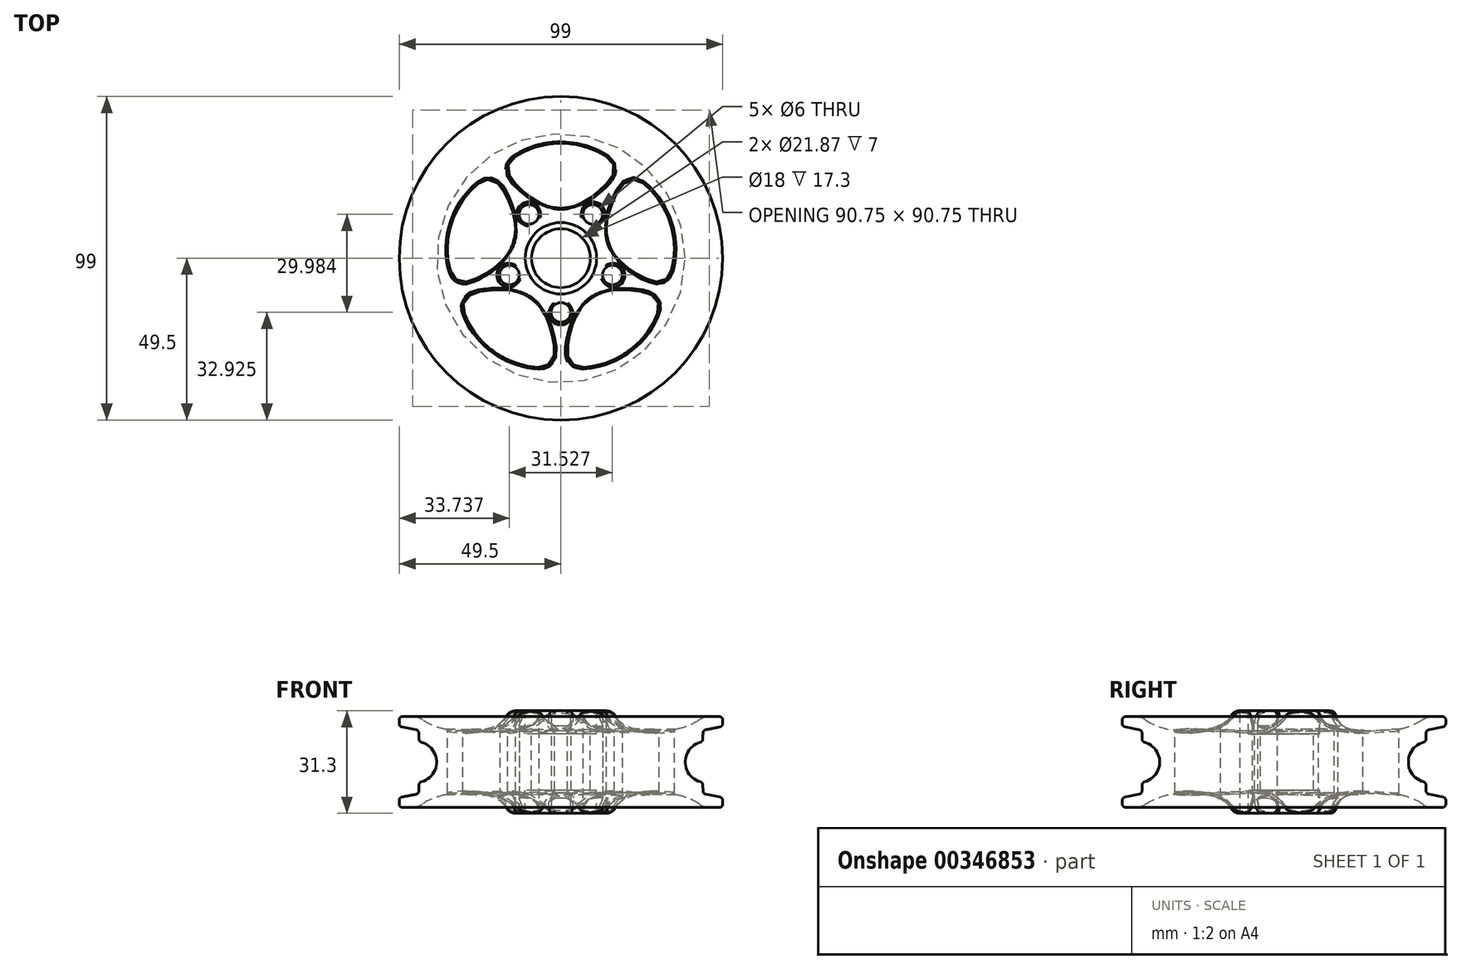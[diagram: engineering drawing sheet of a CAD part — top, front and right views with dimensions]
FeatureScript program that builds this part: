
annotation { "Feature Type Name" : "Feature", "Feature Type Description" : "" }
export const myFeature = defineFeature(function(context is Context, id is Id, definition is map)
    precondition{}
    {
        {
            var Q0;
            Q0=qCreatedBy(makeId("Front.planeOp"),FACE);
            var sketch = newSketch(context, id + "F0", { "sketchPlane" : qUnion([Q0])});
            skLineSegment(sketch, "E0", {"start": v(-10.94, 0) * mm, "end": v(-10.94, 7) * mm});
            skLineSegment(sketch, "E1", {"start": v(-10.94, 24.3) * mm, "end": v(-10.94, 31.3) * mm});
            skLineSegment(sketch, "E2", {"start": v(-10.94, 7) * mm, "end": v(-9, 7) * mm});
            skLineSegment(sketch, "E3", {"start": v(-9, 7) * mm, "end": v(-9, 24.3) * mm});
            skLineSegment(sketch, "E4", {"start": v(-9, 24.3) * mm, "end": v(-10.94, 24.3) * mm});
            skLineSegment(sketch, "E5", {"start": v(-10.94, 31.3) * mm, "end": v(-15.94, 31.3) * mm});
            skLineSegment(sketch, "E6", {"start": v(-10.94, 0) * mm, "end": v(-15.94, 0) * mm});
            skLineSegment(sketch, "E7", {"start": v(-55.59, 1.75) * mm, "end": v(-51.93, 1.75) * mm, "construction": true});
            skLineSegment(sketch, "E8", {"start": v(-9, 15.65) * mm, "end": v(-60.78, 15.65) * mm, "construction": true});
            skLineSegment(sketch, "E9", {"start": v(-55.59, 29.55) * mm, "end": v(-37.99, 29.55) * mm, "construction": true});
            skLineSegment(sketch, "E10", {"start": v(-49.5, 1.75) * mm, "end": v(-43.5, 1.75) * mm});
            skLineSegment(sketch, "E11", {"start": v(-49.5, 1.75) * mm, "end": v(-49.5, 4.75) * mm});
            skLineSegment(sketch, "E12", {"start": v(-49.5, 4.75) * mm, "end": v(-43.5, 5.95) * mm});
            skLineSegment(sketch, "E13", {"start": v(-43.5, 5.95) * mm, "end": v(-43.4, 9.45) * mm});
            skLineSegment(sketch, "E14.MirrorCS", {"start": v(-9, -12.15) * mm, "end": v(-60.78, -12.15) * mm, "construction": true});
            skLineSegment(sketch, "E15.MirrorCS", {"start": v(-43.5, 25.35) * mm, "end": v(-43.4, 21.85) * mm});
            skLineSegment(sketch, "E16.MirrorCS", {"start": v(-49.5, 26.55) * mm, "end": v(-43.5, 25.35) * mm});
            skLineSegment(sketch, "E17.MirrorCS", {"start": v(-49.5, 29.55) * mm, "end": v(-49.5, 26.55) * mm});
            skLineSegment(sketch, "E18.MirrorCS", {"start": v(-49.5, 29.55) * mm, "end": v(-43.5, 29.55) * mm});
            skLineSegment(sketch, "E19", {"start": v(-38.05, 37.76) * mm, "end": v(-38.05, -5.34) * mm, "construction": true});
            skFitSpline(sketch, "E20", {"points": [v(-15.94, 0) * mm, v(-19.3, 4.16) * mm, v(-30.57, 6.15) * mm, v(-38.05, 4.9) * mm, v(-43.5, 1.75) * mm], "startDerivative": vector(-4.85, 18.9) * mm, "endDerivative": vector(-18.06, -19.28) * mm});
            skFitSpline(sketch, "E21.MirrorCS", {"points": [v(-15.94, 31.3) * mm, v(-19.3, 27.14) * mm, v(-30.57, 25.15) * mm, v(-38.05, 26.4) * mm, v(-43.5, 29.55) * mm], "startDerivative": vector(-4.85, -18.9) * mm, "endDerivative": vector(-18.06, 19.28) * mm});
            skArc(sketch, "E22", {"start": v(-43.4, 9.45) * mm, "mid": v(-38.04, 15.65) * mm, "end": v(-43.4, 21.85) * mm});
            skLineSegment(sketch, "E23", {"start": v(0, 53.2) * mm, "end": v(0, -22.44) * mm, "construction": true});
            skSolve(sketch);
        }
        {
            var Q0;
            Q0 = qSketchRegion(id + "F0", true);
            var Q1;
            Q1=makeQuery(id+"F0.imprint","IMPRINT",FACE,{"disambiguationData":[TD([[makeQuery(id+"F0.imprint","IMPRINT",EDGE,{"derivedFrom":sQuery(id+"F0.wireOp",EDGE,"E0")}),1.0]])]});
            var Q2;
            Q2=sQuery(id+"F0.wireOp",EDGE,"E23");
            revolve(context, id + "F1", {"entities" : qUnion([Q0, Q1]), "axis" : qUnion([Q2]), "revolveType" : RevolveType.FULL});
        }
        {
            var Q0;
            Q0=qCreatedBy(makeId("Top.planeOp"),FACE);
            var sketch = newSketch(context, id + "F2", { "sketchPlane" : qUnion([Q0])});
            skPoint(sketch, "E24.center", {"position": v(0, -0.06) * mm});
            skLineSegment(sketch, "E25", {"start": v(0, 56.77) * mm, "end": v(0, 52.22) * mm, "construction": true});
            skFitSpline(sketch, "E26", {"points": [v(5.43, 34.62) * mm, v(-5.43, 34.62) * mm, v(-13.13, 31.63) * mm, v(-15.9, 29.08) * mm, v(-16.02, 25.78) * mm, v(-11.93, 20.8) * mm, v(-5.51, 16.45) * mm, v(0, 15.38) * mm, v(5.51, 16.45) * mm, v(11.93, 20.8) * mm, v(16.02, 25.78) * mm, v(15.9, 29.08) * mm, v(13.13, 31.63) * mm, v(5.43, 34.62) * mm]});
            skFitSpline(sketch, "E27", {"points": [v(34.6, 5.53) * mm, v(31.25, 15.86) * mm, v(26.02, 22.26) * mm, v(22.74, 24.12) * mm, v(19.57, 23.2) * mm, v(16.1, 17.78) * mm, v(13.94, 10.32) * mm, v(14.63, 4.75) * mm, v(17.34, -0.16) * mm, v(23.47, -4.92) * mm, v(29.47, -7.27) * mm, v(32.57, -6.14) * mm, v(34.14, -2.71) * mm, v(34.6, 5.53) * mm]});
            skFitSpline(sketch, "E28", {"points": [v(15.96, -31.2) * mm, v(24.74, -24.82) * mm, v(29.21, -17.87) * mm, v(29.96, -14.18) * mm, v(28.12, -11.44) * mm, v(21.88, -9.82) * mm, v(14.13, -10.07) * mm, v(9.04, -12.44) * mm, v(5.2, -16.55) * mm, v(2.57, -23.85) * mm, v(2.2, -30.28) * mm, v(4.22, -32.88) * mm, v(7.97, -33.3) * mm, v(15.96, -31.2) * mm]});
            skFitSpline(sketch, "E29", {"points": [v(-31.25, 15.86) * mm, v(-34.6, 5.53) * mm, v(-34.14, -2.71) * mm, v(-32.57, -6.14) * mm, v(-29.47, -7.27) * mm, v(-23.47, -4.92) * mm, v(-17.34, -0.16) * mm, v(-14.63, 4.75) * mm, v(-13.94, 10.32) * mm, v(-16.1, 17.78) * mm, v(-19.57, 23.2) * mm, v(-22.74, 24.12) * mm, v(-26.02, 22.26) * mm, v(-31.25, 15.86) * mm]});
            skFitSpline(sketch, "E30", {"points": [v(-24.74, -24.82) * mm, v(-15.96, -31.2) * mm, v(-7.97, -33.3) * mm, v(-4.22, -32.88) * mm, v(-2.2, -30.28) * mm, v(-2.57, -23.85) * mm, v(-5.2, -16.55) * mm, v(-9.04, -12.44) * mm, v(-14.13, -10.07) * mm, v(-21.88, -9.82) * mm, v(-28.12, -11.44) * mm, v(-29.96, -14.18) * mm, v(-29.21, -17.87) * mm, v(-24.74, -24.82) * mm]});
            skCircle(sketch, "E31", {"center": v(0, -16.57) * mm, "radius": 3 * mm});
            skCircle(sketch, "E32.1.0", {"center": v(15.76, -5.12) * mm, "radius": 3 * mm});
            skCircle(sketch, "E32.2.0", {"center": v(9.74, 13.4) * mm, "radius": 3 * mm});
            skCircle(sketch, "E32.3.0", {"center": v(-9.74, 13.4) * mm, "radius": 3 * mm});
            skCircle(sketch, "E32.4.0", {"center": v(-15.76, -5.12) * mm, "radius": 3 * mm});
            skPoint(sketch, "E32.center", {"position": v(0, 0) * mm});
            skSolve(sketch);
        }
        {
            var Q0;
            Q0 = qSketchRegion(id + "F2", true);
            extrude(context, id + "F3", {"entities" : qUnion([Q0]), "operationType" : NewBodyOperationType.REMOVE, "depth" : 44.5 * mm});
        }
        {
            var Q0;
            Q0=makeQuery(id+"F1.opRevolve","SWEPT_FACE",FACE,{"disambiguationData":[OSD([sQuery(id+"F0.wireOp",EDGE,"E17.MirrorCS")])]});
            var Q1;
            Q1=makeQuery(id+"F1.opRevolve","SWEPT_FACE",FACE,{"disambiguationData":[OSD([sQuery(id+"F0.wireOp",EDGE,"E11")])]});
            var Q2;
            Q2=makeQuery(id+"F1.opRevolve","SWEPT_FACE",FACE,{"disambiguationData":[OSD([sQuery(id+"F0.wireOp",EDGE,"E15.MirrorCS")])]});
            var Q3;
            Q3=makeQuery(id+"F1.opRevolve","SWEPT_FACE",FACE,{"disambiguationData":[OSD([sQuery(id+"F0.wireOp",EDGE,"E13")])]});
            fillet(context, id + "F4", {"entities" : qUnion([Q0, Q1, Q2, Q3]), "radius" : 1 * mm, "tangentPropagation" : true, "allowEdgeOverflow" : false});
        }
        {
            var Q0;
            Q0=makeQuery(id+"F1.opRevolve","SWEPT_EDGE",EDGE,{"disambiguationData":[OSD([sQuery(id+"F0.wireOp",EDGE,"E18.MirrorCS"),sQuery(id+"F0.wireOp",EDGE,"E21.MirrorCS")])]});
            var Q1;
            Q1=makeQuery(id+"F1.opRevolve","SWEPT_EDGE",EDGE,{"disambiguationData":[OSD([sQuery(id+"F0.wireOp",EDGE,"E10"),sQuery(id+"F0.wireOp",EDGE,"E20")])]});
            fillet(context, id + "F5", {"entities" : qUnion([Q0, Q1]), "radius" : 5 * mm, "tangentPropagation" : true, "allowEdgeOverflow" : false});
        }
        {
            var Q0;
            Q0=makeQuery(id+"F1.opRevolve","SWEPT_EDGE",EDGE,{"disambiguationData":[OSD([sQuery(id+"F0.wireOp",EDGE,"E5"),sQuery(id+"F0.wireOp",EDGE,"E21.MirrorCS")])]});
            var Q1;
            Q1=makeQuery(id+"F1.opRevolve","SWEPT_EDGE",EDGE,{"disambiguationData":[OSD([sQuery(id+"F0.wireOp",EDGE,"E6"),sQuery(id+"F0.wireOp",EDGE,"E20")])]});
            fillet(context, id + "F6", {"entities" : qUnion([Q0, Q1]), "radius" : 3 * mm, "tangentPropagation" : true, "allowEdgeOverflow" : false});
        }
        {
            var Q0;
            Q0=makeQuery(id+"F3.boolean.opBoolean","COPY",FACE,{"derivedFrom":makeQuery(id+"F3.opExtrude","SWEPT_FACE",FACE,{"disambiguationData":[OSD([sQuery(id+"F2.wireOp",EDGE,"E26")])]})});
            var Q1;
            Q1=makeQuery(id+"F3.boolean.opBoolean","COPY",FACE,{"derivedFrom":makeQuery(id+"F3.opExtrude","SWEPT_FACE",FACE,{"disambiguationData":[OSD([sQuery(id+"F2.wireOp",EDGE,"E32.3.0")])]})});
            var Q2;
            Q2=makeQuery(id+"F3.boolean.opBoolean","COPY",FACE,{"derivedFrom":makeQuery(id+"F3.opExtrude","SWEPT_FACE",FACE,{"disambiguationData":[OSD([sQuery(id+"F2.wireOp",EDGE,"E32.2.0")])]})});
            var Q3;
            Q3=makeQuery(id+"F3.boolean.opBoolean","COPY",FACE,{"derivedFrom":makeQuery(id+"F3.opExtrude","SWEPT_FACE",FACE,{"disambiguationData":[OSD([sQuery(id+"F2.wireOp",EDGE,"E27")])]})});
            var Q4;
            Q4=makeQuery(id+"F3.boolean.opBoolean","COPY",FACE,{"derivedFrom":makeQuery(id+"F3.opExtrude","SWEPT_FACE",FACE,{"disambiguationData":[OSD([sQuery(id+"F2.wireOp",EDGE,"E29")])]})});
            var Q5;
            Q5=makeQuery(id+"F3.boolean.opBoolean","COPY",FACE,{"derivedFrom":makeQuery(id+"F3.opExtrude","SWEPT_FACE",FACE,{"disambiguationData":[OSD([sQuery(id+"F2.wireOp",EDGE,"E32.4.0")])]})});
            var Q6;
            Q6=makeQuery(id+"F3.boolean.opBoolean","COPY",FACE,{"derivedFrom":makeQuery(id+"F3.opExtrude","SWEPT_FACE",FACE,{"disambiguationData":[OSD([sQuery(id+"F2.wireOp",EDGE,"E31")])]})});
            var Q7;
            Q7=makeQuery(id+"F3.boolean.opBoolean","COPY",FACE,{"derivedFrom":makeQuery(id+"F3.opExtrude","SWEPT_FACE",FACE,{"disambiguationData":[OSD([sQuery(id+"F2.wireOp",EDGE,"E32.1.0")])]})});
            var Q8;
            Q8=makeQuery(id+"F3.boolean.opBoolean","COPY",FACE,{"derivedFrom":makeQuery(id+"F3.opExtrude","SWEPT_FACE",FACE,{"disambiguationData":[OSD([sQuery(id+"F2.wireOp",EDGE,"E28")])]})});
            var Q9;
            Q9=makeQuery(id+"F3.boolean.opBoolean","COPY",FACE,{"derivedFrom":makeQuery(id+"F3.opExtrude","SWEPT_FACE",FACE,{"disambiguationData":[OSD([sQuery(id+"F2.wireOp",EDGE,"E30")])]})});
            fillet(context, id + "F7", {"entities" : qUnion([Q0, Q1, Q2, Q3, Q4, Q5, Q6, Q7, Q8, Q9]), "radius" : 0.6 * mm, "tangentPropagation" : true, "allowEdgeOverflow" : false});
        }
    });
